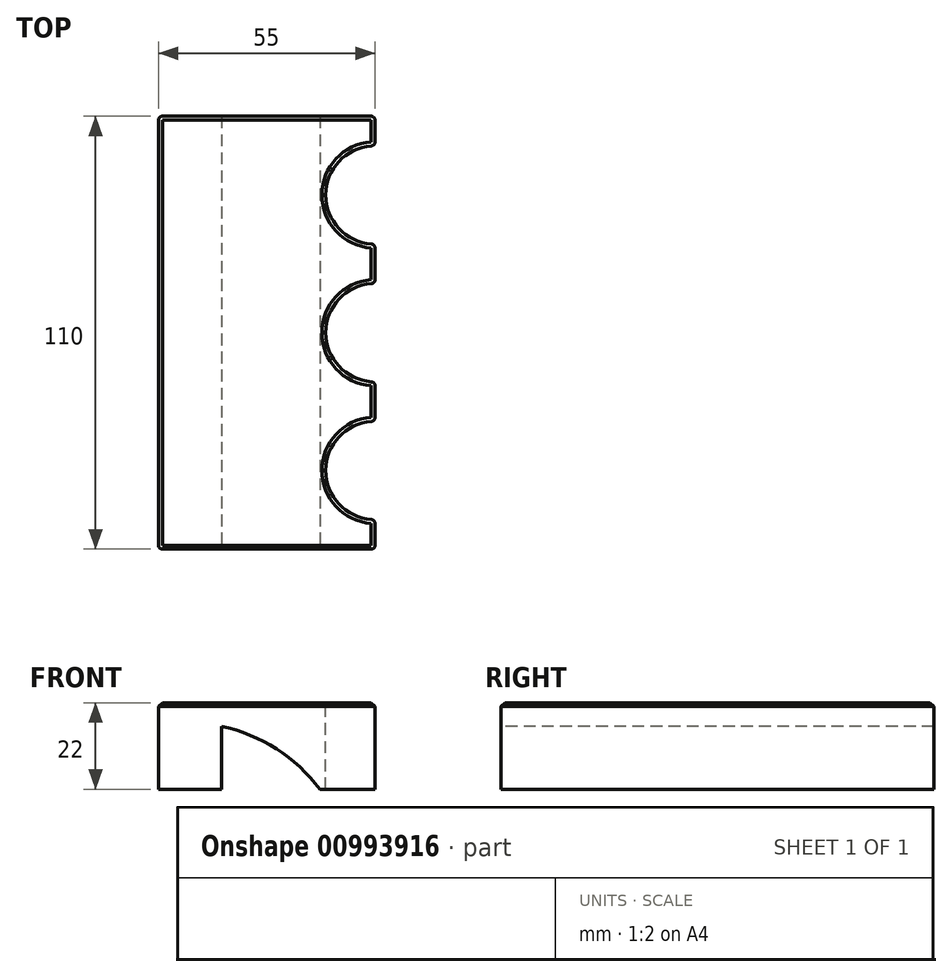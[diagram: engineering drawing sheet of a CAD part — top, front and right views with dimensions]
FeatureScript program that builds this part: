
annotation { "Feature Type Name" : "Feature", "Feature Type Description" : "" }
export const myFeature = defineFeature(function(context is Context, id is Id, definition is map)
    precondition{}
    {
        {
            var Q0;
            Q0=qCreatedBy(makeId("Top.planeOp"),FACE);
            var sketch = newSketch(context, id + "F0", { "sketchPlane" : qUnion([Q0])});
            skLineSegment(sketch, "E0.bottom", {"start": v(27.5, -55) * mm, "end": v(-27.5, -55) * mm});
            skLineSegment(sketch, "E0.top", {"start": v(27.5, 55) * mm, "end": v(-27.5, 55) * mm});
            skLineSegment(sketch, "E0.left", {"start": v(27.5, -55) * mm, "end": v(27.5, 55) * mm});
            skLineSegment(sketch, "E0.right", {"start": v(-27.5, -55) * mm, "end": v(-27.5, 55) * mm});
            skPoint(sketch, "E0.middle", {"position": v(0, 0) * mm});
            skSolve(sketch);
        }
        {
            var Q0;
            Q0 = qSketchRegion(id + "F0", true);
            extrude(context, id + "F1", {"entities" : qUnion([Q0]), "depth" : 22 * mm, "offsetDistance" : 25 * mm});
        }
        {
            var Q0;
            Q0=makeQuery(id+"F1.opExtrude","CAP_FACE",FACE,{"disambiguationData":[OSD([sQuery(id+"F0.wireOp",EDGE,"E0.bottom"),sQuery(id+"F0.wireOp",EDGE,"E0.top"),sQuery(id+"F0.wireOp",EDGE,"E0.left"),sQuery(id+"F0.wireOp",EDGE,"E0.right")])],"isStart":false});
            var sketch = newSketch(context, id + "F2", { "sketchPlane" : qUnion([Q0])});
            skCircle(sketch, "E1", {"center": v(27.5, 0) * mm, "radius": 12.5 * mm});
            skCircle(sketch, "E2", {"center": v(27.5, 35) * mm, "radius": 12.5 * mm});
            skCircle(sketch, "E3", {"center": v(27.5, -35) * mm, "radius": 12.5 * mm});
            skSolve(sketch);
        }
        {
            var Q0;
            Q0 = qSketchRegion(id + "F2", true);
            extrude(context, id + "F3", {"entities" : qUnion([Q0]), "operationType" : NewBodyOperationType.REMOVE, "oppositeDirection" : true, "depth" : 25 * mm, "offsetDistance" : 25 * mm});
        }
        {
            var Q0;
            Q0=makeQuery(id+"F1.opExtrude","SWEPT_FACE",FACE,{"disambiguationData":[OSD([sQuery(id+"F0.wireOp",EDGE,"E0.bottom")])]});
            var sketch = newSketch(context, id + "F4", { "sketchPlane" : qUnion([Q0])});
            skLineSegment(sketch, "E4", {"start": v(-11.5, 0) * mm, "end": v(-11.5, 16) * mm});
            skLineSegment(sketch, "E5", {"start": v(-11.5, 0) * mm, "end": v(13.5, 0) * mm});
            skArc(sketch, "E6", {"start": v(13.5, 0) * mm, "mid": v(2.44, 10.25) * mm, "end": v(-11.5, 16) * mm});
            skSolve(sketch);
        }
        {
            var Q0;
            Q0=makeQuery(id+"F4.imprint","IMPRINT",FACE,{"disambiguationData":[TD([[makeQuery(id+"F4.imprint","IMPRINT",EDGE,{"derivedFrom":sQuery(id+"F4.wireOp",EDGE,"E4")}),-1.0]])]});
            extrude(context, id + "F5", {"entities" : qUnion([Q0]), "operationType" : NewBodyOperationType.REMOVE, "endBound" : BoundingType.THROUGH_ALL, "oppositeDirection" : true, "depth" : 25 * mm, "offsetDistance" : 25 * mm});
        }
        {
            var Q0;
            Q0=makeQuery(id+"F3.boolean.opBoolean","INTERSECT",EDGE,{"disambiguationData":[OD(0.0)],"derivedFrom":[makeQuery(id+"F1.opExtrude","SWEPT_FACE",FACE,{"disambiguationData":[OSD([sQuery(id+"F0.wireOp",EDGE,"E0.left")])]}),makeQuery(id+"F3.opExtrude","SWEPT_FACE",FACE,{"disambiguationData":[OSD([sQuery(id+"F2.wireOp",EDGE,"E1")])]})]});
            var Q1;
            Q1=makeQuery(id+"F3.boolean.opBoolean","INTERSECT",EDGE,{"disambiguationData":[OD(1.0)],"derivedFrom":[makeQuery(id+"F1.opExtrude","SWEPT_FACE",FACE,{"disambiguationData":[OSD([sQuery(id+"F0.wireOp",EDGE,"E0.left")])]}),makeQuery(id+"F3.opExtrude","SWEPT_FACE",FACE,{"disambiguationData":[OSD([sQuery(id+"F2.wireOp",EDGE,"E2")])]})]});
            var Q2;
            Q2=makeQuery(id+"F3.boolean.opBoolean","INTERSECT",EDGE,{"disambiguationData":[OD(0.0)],"derivedFrom":[makeQuery(id+"F1.opExtrude","SWEPT_FACE",FACE,{"disambiguationData":[OSD([sQuery(id+"F0.wireOp",EDGE,"E0.left")])]}),makeQuery(id+"F3.opExtrude","SWEPT_FACE",FACE,{"disambiguationData":[OSD([sQuery(id+"F2.wireOp",EDGE,"E2")])]})]});
            var Q3;
            Q3=makeQuery(id+"F3.boolean.opBoolean","INTERSECT",EDGE,{"disambiguationData":[OD(1.0)],"derivedFrom":[makeQuery(id+"F1.opExtrude","SWEPT_FACE",FACE,{"disambiguationData":[OSD([sQuery(id+"F0.wireOp",EDGE,"E0.left")])]}),makeQuery(id+"F3.opExtrude","SWEPT_FACE",FACE,{"disambiguationData":[OSD([sQuery(id+"F2.wireOp",EDGE,"E1")])]})]});
            var Q4;
            Q4=makeQuery(id+"F3.boolean.opBoolean","INTERSECT",EDGE,{"disambiguationData":[OD(1.0)],"derivedFrom":[makeQuery(id+"F1.opExtrude","SWEPT_FACE",FACE,{"disambiguationData":[OSD([sQuery(id+"F0.wireOp",EDGE,"E0.left")])]}),makeQuery(id+"F3.opExtrude","SWEPT_FACE",FACE,{"disambiguationData":[OSD([sQuery(id+"F2.wireOp",EDGE,"E3")])]})]});
            var Q5;
            Q5=makeQuery(id+"F3.boolean.opBoolean","INTERSECT",EDGE,{"disambiguationData":[OD(0.0)],"derivedFrom":[makeQuery(id+"F1.opExtrude","SWEPT_FACE",FACE,{"disambiguationData":[OSD([sQuery(id+"F0.wireOp",EDGE,"E0.left")])]}),makeQuery(id+"F3.opExtrude","SWEPT_FACE",FACE,{"disambiguationData":[OSD([sQuery(id+"F2.wireOp",EDGE,"E3")])]})]});
            var Q6;
            Q6=makeQuery(id+"F1.opExtrude","SWEPT_EDGE",EDGE,{"disambiguationData":[OSD([sQuery(id+"F0.wireOp",EDGE,"E0.bottom"),sQuery(id+"F0.wireOp",EDGE,"E0.left")])]});
            var Q7;
            Q7=makeQuery(id+"F1.opExtrude","SWEPT_EDGE",EDGE,{"disambiguationData":[OSD([sQuery(id+"F0.wireOp",EDGE,"E0.bottom"),sQuery(id+"F0.wireOp",EDGE,"E0.right")])]});
            var Q8;
            Q8=makeQuery(id+"F1.opExtrude","SWEPT_EDGE",EDGE,{"disambiguationData":[OSD([sQuery(id+"F0.wireOp",EDGE,"E0.top"),sQuery(id+"F0.wireOp",EDGE,"E0.left")])]});
            var Q9;
            Q9=makeQuery(id+"F1.opExtrude","SWEPT_EDGE",EDGE,{"disambiguationData":[OSD([sQuery(id+"F0.wireOp",EDGE,"E0.top"),sQuery(id+"F0.wireOp",EDGE,"E0.right")])]});
            fillet(context, id + "F6", {"entities" : qUnion([Q0, Q1, Q2, Q3, Q4, Q5, Q6, Q7, Q8, Q9]), "radius" : 1 * mm, "tangentPropagation" : true, "allowEdgeOverflow" : false});
        }
        {
            var Q0;
            Q0=makeQuery(id+"F1.opExtrude","CAP_FACE",FACE,{"disambiguationData":[OSD([sQuery(id+"F0.wireOp",EDGE,"E0.bottom"),sQuery(id+"F0.wireOp",EDGE,"E0.top"),sQuery(id+"F0.wireOp",EDGE,"E0.left"),sQuery(id+"F0.wireOp",EDGE,"E0.right")])],"isStart":false});
            chamfer(context, id + "F7", {"entities" : qUnion([Q0]), "width" : 1 * mm, "tangentPropagation" : true});
        }
    });
